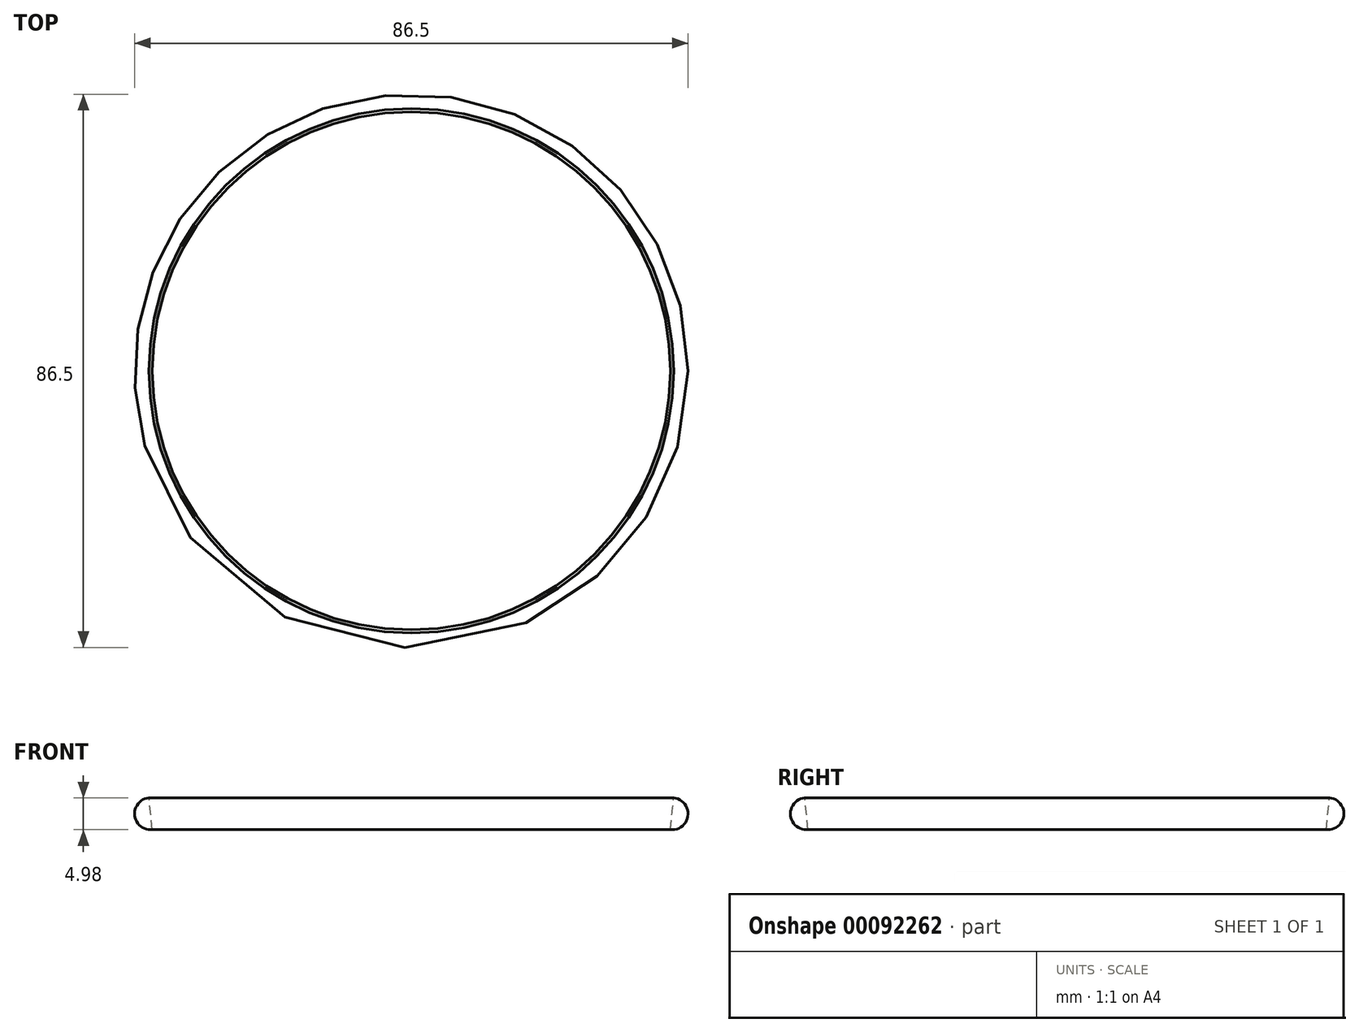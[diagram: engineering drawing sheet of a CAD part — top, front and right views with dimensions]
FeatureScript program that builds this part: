
annotation { "Feature Type Name" : "Feature", "Feature Type Description" : "" }
export const myFeature = defineFeature(function(context is Context, id is Id, definition is map)
    precondition{}
    {
        {
            var Q0;
            Q0=qCreatedBy(makeId("Front.planeOp"),FACE);
            var sketch = newSketch(context, id + "F0", { "sketchPlane" : qUnion([Q0])});
            skLineSegment(sketch, "E0", {"start": v(31, -51.96) * mm, "end": v(41, 46.53) * mm});
            skArc(sketch, "E1", {"start": v(40.5, 41.56) * mm, "mid": v(43.23, 43.8) * mm, "end": v(41, 46.53) * mm});
            skLineSegment(sketch, "E2", {"start": v(0, 20.44) * mm, "end": v(0, -9.52) * mm, "construction": true});
            skLineSegment(sketch, "E3", {"start": v(0, -41.96) * mm, "end": v(32.02, -41.96) * mm});
            skSolve(sketch);
        }
        {
            var Q0;
            Q0 = qSketchRegion(id + "F0", true);
            var Q1;
            Q1=sQuery(id+"F0.wireOp",EDGE,"E0");
            var Q2;
            Q2=sQuery(id+"F0.wireOp",EDGE,"E2");
            revolve(context, id + "F1", {"bodyType" : ToolBodyType.SURFACE, "entities" : qUnion([Q0]), "surfaceEntities" : qUnion([Q1]), "axis" : qUnion([Q2]), "revolveType" : RevolveType.FULL});
        }
        {
            var Q0;
            Q0=sQuery(id+"F0.wireOp",EDGE,"E3");
            var Q1;
            Q1=sQuery(id+"F0.wireOp",EDGE,"E2");
            revolve(context, id + "F2", {"bodyType" : ToolBodyType.SURFACE, "surfaceEntities" : qUnion([Q0]), "axis" : qUnion([Q1]), "revolveType" : RevolveType.FULL});
        }
        {
            var Q0;
            {var subQ0=sQuery(id+"F0.wireOp",EDGE,"E1");Q0=makeQuery(id+"F0.imprint","IMPRINT",FACE,{"disambiguationData":[TD([[makeQuery(id+"F0.imprint","IMPRINT",EDGE,{"derivedFrom":subQ0}),1.0]])]});}
            var Q1;
            Q1=sQuery(id+"F0.wireOp",EDGE,"E2");
            revolve(context, id + "F3", {"entities" : qUnion([Q0]), "axis" : qUnion([Q1]), "revolveType" : RevolveType.FULL});
        }
    });
